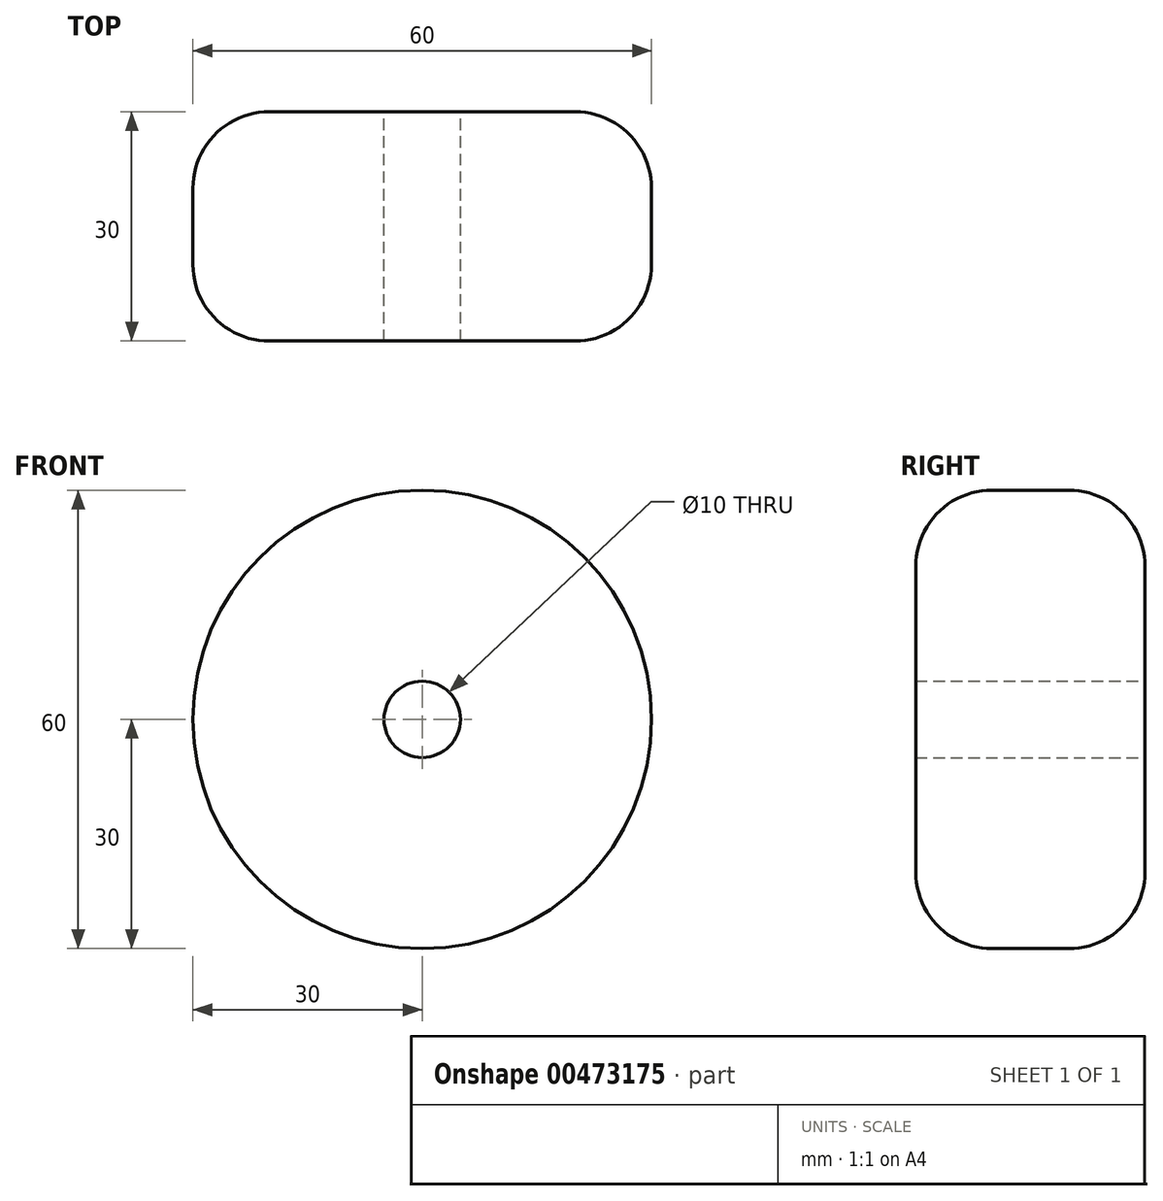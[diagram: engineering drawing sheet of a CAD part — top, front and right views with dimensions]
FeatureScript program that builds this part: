
annotation { "Feature Type Name" : "Feature", "Feature Type Description" : "" }
export const myFeature = defineFeature(function(context is Context, id is Id, definition is map)
    precondition{}
    {
        {
            assignVariable(context, id + "F0", {"name" : "Epaisseur_Galette", "anyValue" : 30});
        }
        {
            var Q0;
            Q0=qCreatedBy(makeId("Front.planeOp"),FACE);
            var sketch = newSketch(context, id + "F1", { "sketchPlane" : qUnion([Q0])});
            skCircle(sketch, "E0", {"center": v(0, 0) * mm, "radius": 30 * mm});
            skCircle(sketch, "E1", {"center": v(0, 0) * mm, "radius": 5 * mm});
            skSolve(sketch);
        }
        {
            var Q0;
            Q0 = qSketchRegion(id + "F1", true);
            extrude(context, id + "F2", {"entities" : qUnion([Q0]), "depth" : (getVariable(context, 'Epaisseur_Galette')) * mm, "offsetDistance" : 25 * mm, "symmetric" : true});
        }
        {
            var Q0;
            Q0=makeQuery(id+"F2.opExtrude","CAP_EDGE",EDGE,{"disambiguationData":[OSD([sQuery(id+"F1.wireOp",EDGE,"E0")])],"isStart":false});
            var Q1;
            Q1=makeQuery(id+"F2.opExtrude","CAP_EDGE",EDGE,{"disambiguationData":[OSD([sQuery(id+"F1.wireOp",EDGE,"E0")])],"isStart":true});
            fillet(context, id + "F3", {"entities" : qUnion([Q0, Q1]), "radius" : 10 * mm, "tangentPropagation" : true, "allowEdgeOverflow" : false});
        }
    });
